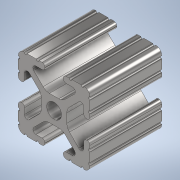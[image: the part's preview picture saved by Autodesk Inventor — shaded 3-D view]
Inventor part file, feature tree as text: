
AUTODESK INVENTOR PART (.ipt)
format: ipt  version: 2020 (Build 240168000, 168)  size: 245,760 bytes
history: native  units: in
note: dims shown in document units (in); Inventor stores cm internally (conversion verified against a paired STEP export)
features: extrude x1, sketch x1
ambient origin geometry x8: Origin, YZ Plane, XZ Plane, XY Plane, X Axis, Y Axis, Z Axis, Center Point
bodies: Solid1 (feature_tree)
feature tree (2):
  extrude  "Extrusion1"  [1 undecoded]
  sketch  "Sketch1"  dims[d0=1.0in d1=0.0in]
note: 1 required parameter value undecoded (feature->parameter linkage not recoverable at this tier; creation-order binding heuristic only, values carry confidence <= 0.55)
